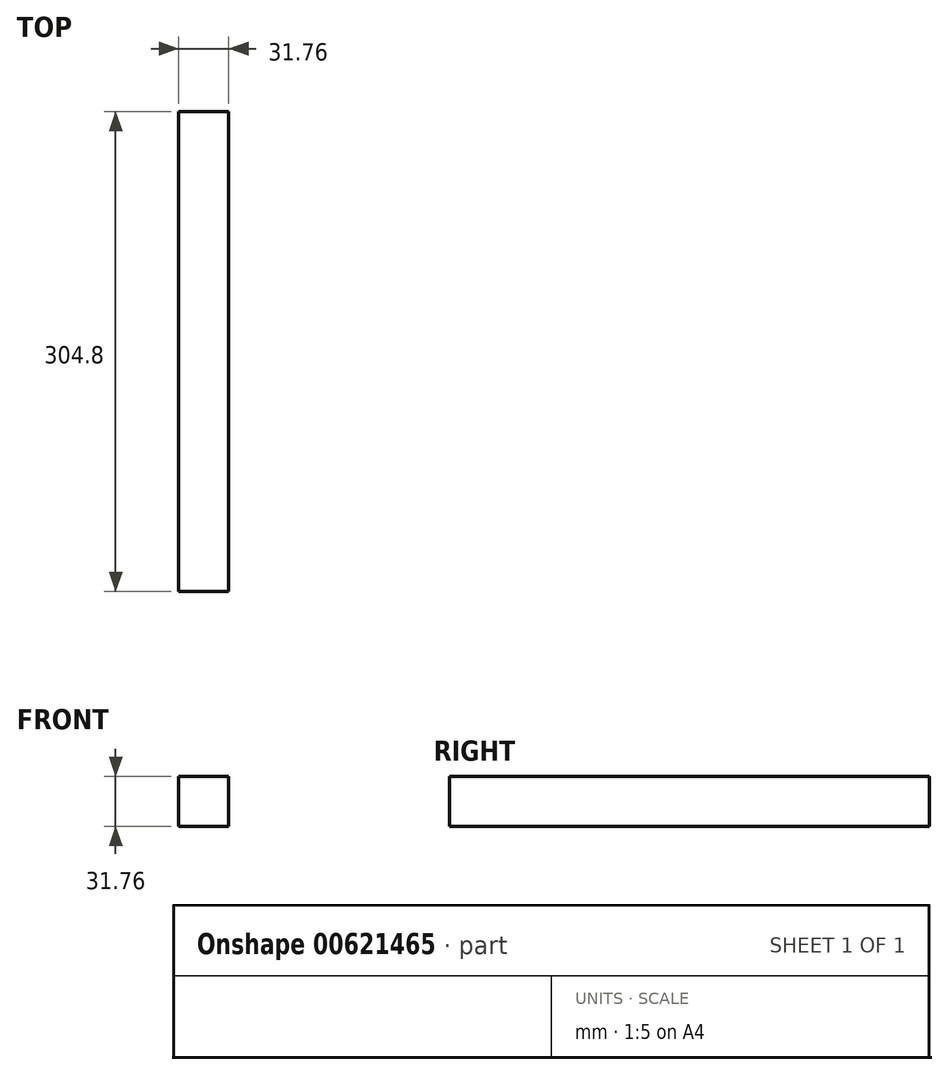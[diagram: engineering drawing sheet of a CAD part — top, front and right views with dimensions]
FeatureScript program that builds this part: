
annotation { "Feature Type Name" : "Feature", "Feature Type Description" : "" }
export const myFeature = defineFeature(function(context is Context, id is Id, definition is map)
    precondition{}
    {
        {
            var Q0;
            Q0=qCreatedBy(makeId("Front.planeOp"),FACE);
            var sketch = newSketch(context, id + "F0", { "sketchPlane" : qUnion([Q0])});
            skLineSegment(sketch, "E0.bottom", {"start": v(15.88, 15.88) * mm, "end": v(-15.88, 15.88) * mm});
            skLineSegment(sketch, "E0.top", {"start": v(15.88, -15.88) * mm, "end": v(-15.88, -15.88) * mm});
            skLineSegment(sketch, "E0.left", {"start": v(15.88, 15.88) * mm, "end": v(15.88, -15.88) * mm});
            skLineSegment(sketch, "E0.right", {"start": v(-15.88, 15.87) * mm, "end": v(-15.88, -15.88) * mm});
            skPoint(sketch, "E0.middle", {"position": v(0, 0) * mm});
            skSolve(sketch);
        }
        {
            var Q0;
            Q0 = qSketchRegion(id + "F0", true);
            extrude(context, id + "F1", {"entities" : qUnion([Q0]), "depth" : 304.8 * mm, "offsetDistance" : 25.4 * mm});
        }
    });
